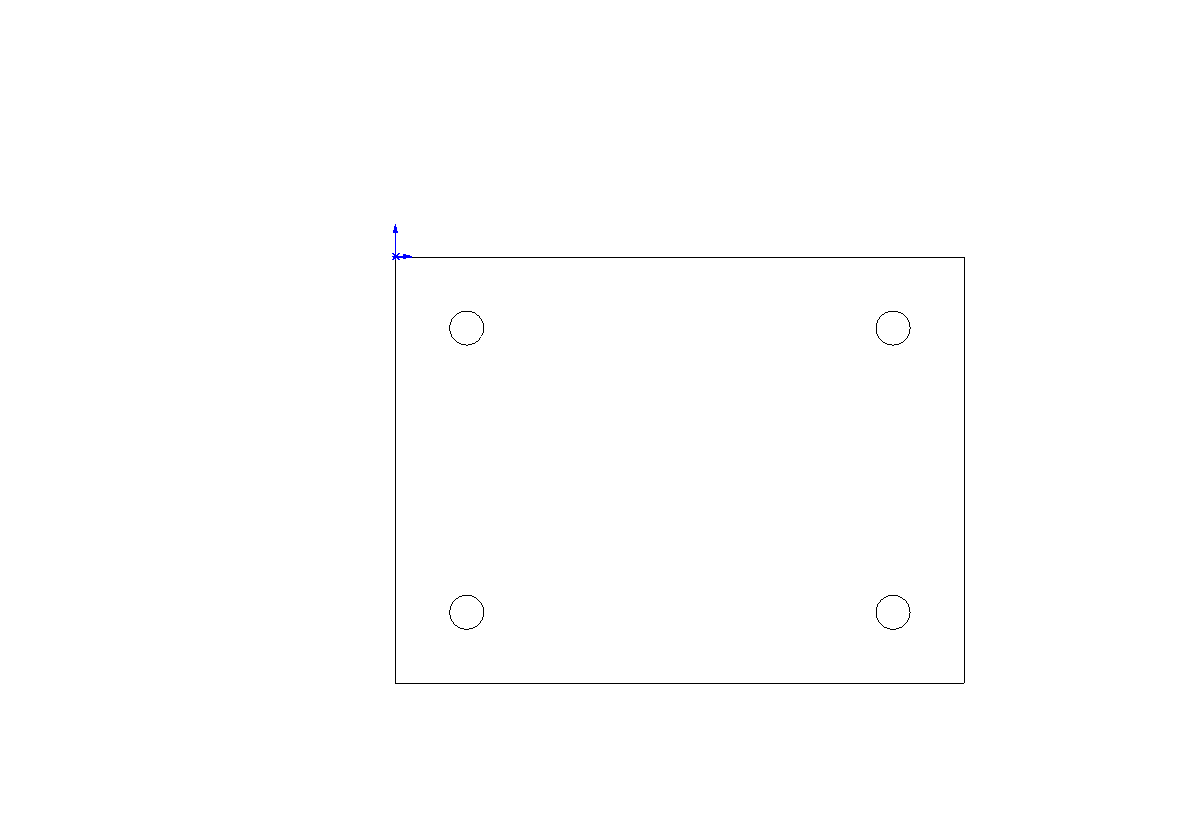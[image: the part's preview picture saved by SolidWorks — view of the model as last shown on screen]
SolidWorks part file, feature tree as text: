
SOLIDWORKS PART (.sldprt)
format: sldprt  version: not decoded by parser v0  size: 143,872 bytes
history: native  units: mm
features: sketch x2, material x1, extrude x1, cut_extrude x1, pattern_linear x1 (+13 scaffold rows collapsed)
feature tree (19):
  scaffold x13  (default folders/planes/origin — collapsed)
  material  "Material <not specified>"
  sketch  "Sketch1"  dims[D1=38.1mm D2=50.8mm]
  extrude  "Extrude1"  Depth=1.6002mm
  sketch  "Sketch2"  dims[D1=3.048mm D2=6.35mm D3=6.35mm]
  cut_extrude  "Cut-Extrude1"  Depth=1.6002mm
  pattern_linear  "LPattern1"  Count1=2 Count2=2 Spacing1=38.1mm Spacing2=25.4mm
decode coverage: 5 of 5 modeling features carry decoded parameters
note: suppression state not decoded; provenance and decode notes live in map.json
